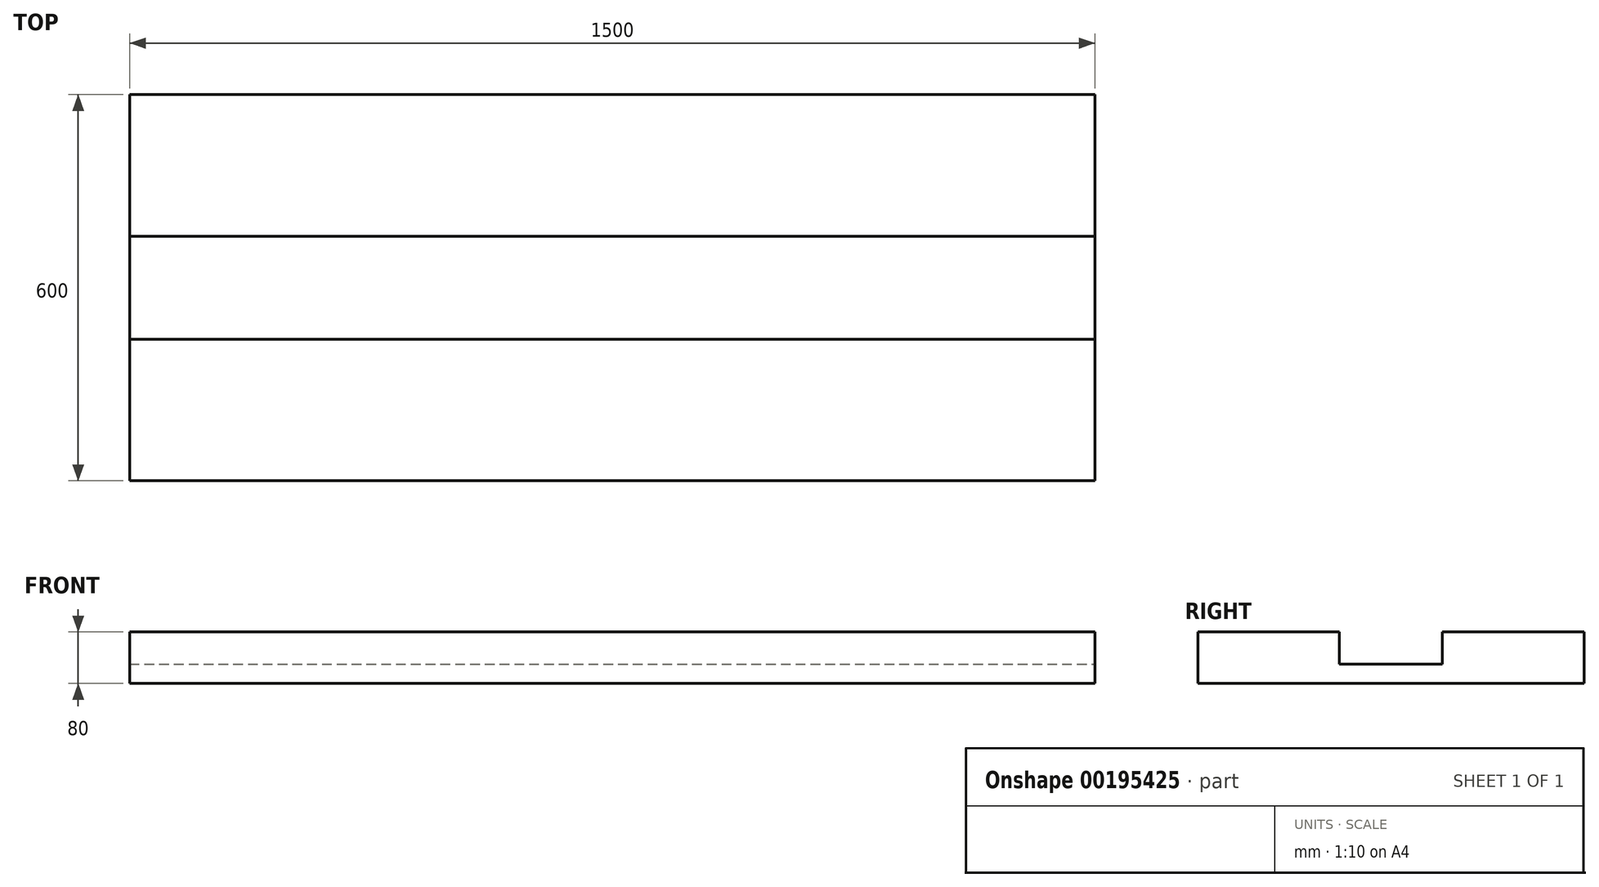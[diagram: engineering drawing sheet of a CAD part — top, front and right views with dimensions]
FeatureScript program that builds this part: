
annotation { "Feature Type Name" : "Feature", "Feature Type Description" : "" }
export const myFeature = defineFeature(function(context is Context, id is Id, definition is map)
    precondition{}
    {
        {
            var Q0;
            Q0=qCreatedBy(makeId("Top.planeOp"),FACE);
            var sketch = newSketch(context, id + "F0", { "sketchPlane" : qUnion([Q0])});
            skLineSegment(sketch, "E0.bottom", {"start": v(750, -300) * mm, "end": v(-750, -300) * mm});
            skLineSegment(sketch, "E0.top", {"start": v(750, 300) * mm, "end": v(-750, 300) * mm});
            skLineSegment(sketch, "E0.left", {"start": v(750, -300) * mm, "end": v(750, 300) * mm});
            skLineSegment(sketch, "E0.right", {"start": v(-750, -300) * mm, "end": v(-750, 300) * mm});
            skPoint(sketch, "E0.middle", {"position": v(0, 0) * mm});
            skSolve(sketch);
        }
        {
            var Q0;
            Q0=makeQuery(id+"F0.imprint","IMPRINT",FACE,{"disambiguationData":[TD([[makeQuery(id+"F0.imprint","IMPRINT",EDGE,{"derivedFrom":sQuery(id+"F0.wireOp",EDGE,"E0.bottom")}),-1.0]])]});
            extrude(context, id + "F1", {"entities" : qUnion([Q0]), "depth" : 80 * mm});
        }
        {
            var Q0;
            Q0=makeQuery(id+"F1.opExtrude","CAP_FACE",FACE,{"disambiguationData":[OSD([sQuery(id+"F0.wireOp",EDGE,"E0.bottom"),sQuery(id+"F0.wireOp",EDGE,"E0.top"),sQuery(id+"F0.wireOp",EDGE,"E0.left"),sQuery(id+"F0.wireOp",EDGE,"E0.right")])],"isStart":false});
            var sketch = newSketch(context, id + "F2", { "sketchPlane" : qUnion([Q0])});
            skLineSegment(sketch, "E1.0.left", {"start": v(-750, 80) * mm, "end": v(750, 80) * mm});
            skLineSegment(sketch, "E1.0.right", {"start": v(-750, -80) * mm, "end": v(750, -80) * mm});
            skLineSegment(sketch, "E2", {"start": v(750, 80) * mm, "end": v(750, -80) * mm});
            skLineSegment(sketch, "E3", {"start": v(-750, 80) * mm, "end": v(-750, -80) * mm});
            skSolve(sketch);
        }
        {
            var Q0;
            Q0=makeQuery(id+"F2.imprint","IMPRINT",FACE,{"disambiguationData":[TD([[makeQuery(id+"F2.imprint","IMPRINT",EDGE,{"derivedFrom":sQuery(id+"F2.wireOp",EDGE,"E1.0.left")}),-1.0]])]});
            extrude(context, id + "F3", {"entities" : qUnion([Q0]), "operationType" : NewBodyOperationType.REMOVE, "oppositeDirection" : true, "depth" : 50 * mm});
        }
    });
